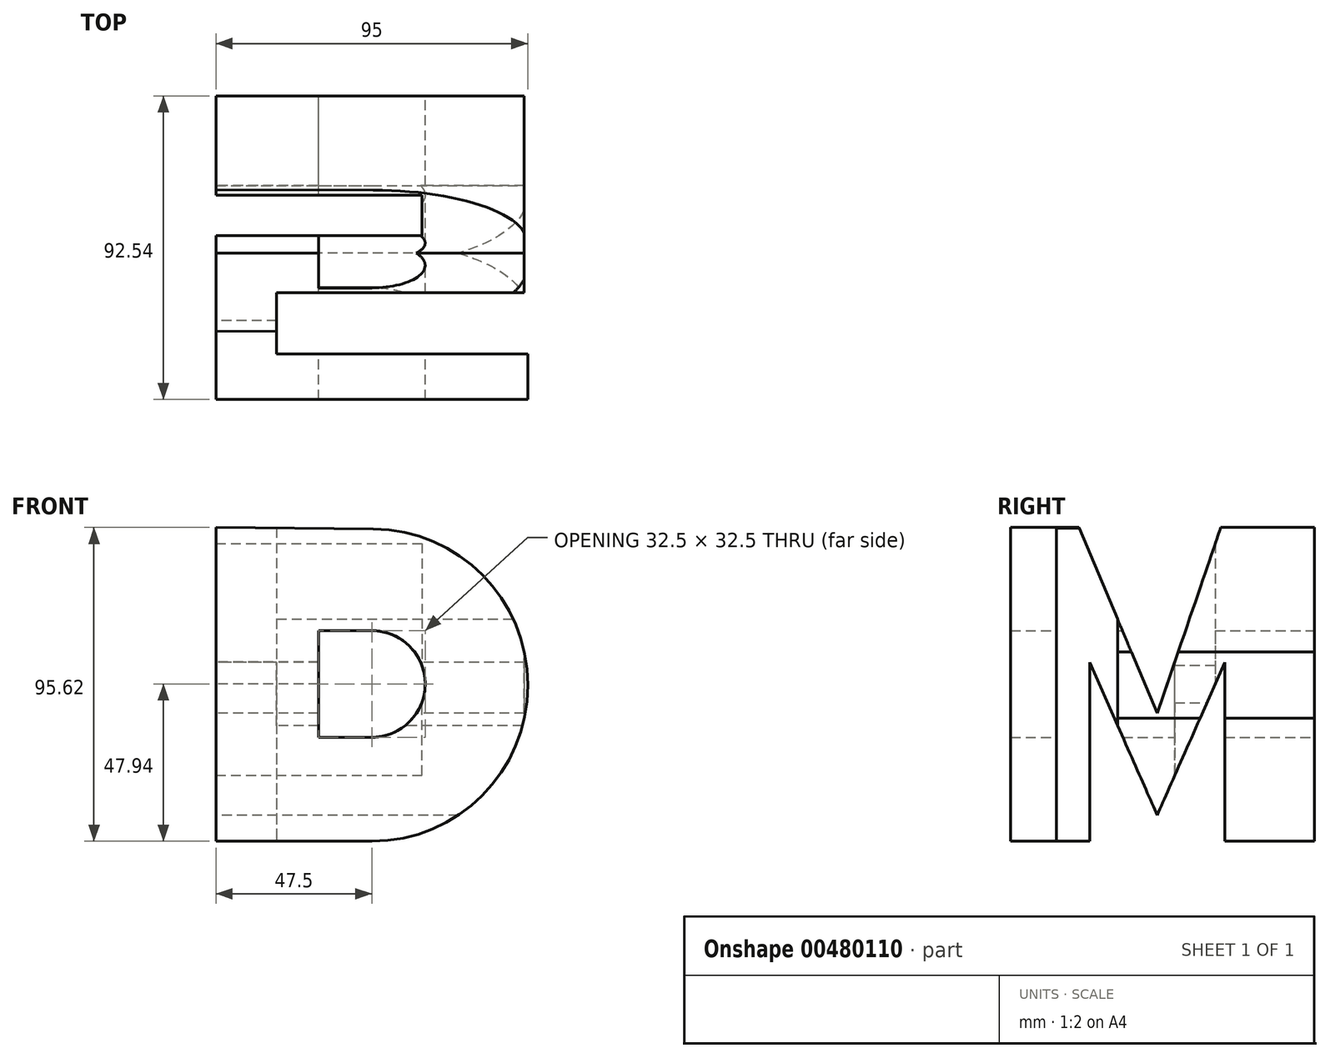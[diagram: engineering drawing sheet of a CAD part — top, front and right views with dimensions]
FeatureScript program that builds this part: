
annotation { "Feature Type Name" : "Feature", "Feature Type Description" : "" }
export const myFeature = defineFeature(function(context is Context, id is Id, definition is map)
    precondition{}
    {
        {
            var Q0;
            Q0=qCreatedBy(makeId("Top.planeOp"),FACE);
            var sketch = newSketch(context, id + "F0", { "sketchPlane" : qUnion([Q0])});
            skLineSegment(sketch, "E0.bottom", {"start": v(50, 50) * mm, "end": v(-50, 50) * mm, "construction": true});
            skLineSegment(sketch, "E0.top", {"start": v(50, -50) * mm, "end": v(-50, -50) * mm, "construction": true});
            skLineSegment(sketch, "E0.left", {"start": v(50, 50) * mm, "end": v(50, -50) * mm, "construction": true});
            skLineSegment(sketch, "E0.right", {"start": v(-50, 50) * mm, "end": v(-50, -50) * mm, "construction": true});
            skPoint(sketch, "E0.middle", {"position": v(0, 0) * mm});
            skLineSegment(sketch, "E1", {"start": v(30, -36.1) * mm, "end": v(-29, -36.1) * mm});
            skLineSegment(sketch, "E2", {"start": v(-29, -36.1) * mm, "end": v(-29, -17.46) * mm});
            skLineSegment(sketch, "E3", {"start": v(-29, -17.46) * mm, "end": v(30, -17.46) * mm});
            skLineSegment(sketch, "E4", {"start": v(30, 42.54) * mm, "end": v(-50, 42.54) * mm});
            skLineSegment(sketch, "E5", {"start": v(-50, 42.54) * mm, "end": v(-50, 12.32) * mm});
            skLineSegment(sketch, "E6", {"start": v(-50, 12.32) * mm, "end": v(15.22, 12.32) * mm});
            skLineSegment(sketch, "E7", {"start": v(15.22, 0) * mm, "end": v(-50, 0) * mm});
            skLineSegment(sketch, "E8", {"start": v(-50, 0) * mm, "end": v(-50, -50) * mm});
            skLineSegment(sketch, "E9", {"start": v(-50, -50) * mm, "end": v(30, -50) * mm});
            skLineSegment(sketch, "E10", {"start": v(15.22, 12.32) * mm, "end": v(15.22, 0) * mm});
            skLineSegment(sketch, "E11", {"start": v(30, -50) * mm, "end": v(50, -50) * mm});
            skLineSegment(sketch, "E12", {"start": v(30, -36.1) * mm, "end": v(50, -36.1) * mm});
            skLineSegment(sketch, "E13", {"start": v(50, -36.1) * mm, "end": v(50, -50) * mm});
            skLineSegment(sketch, "E14", {"start": v(30, -17.46) * mm, "end": v(46.44, -17.46) * mm});
            skLineSegment(sketch, "E15", {"start": v(46.44, -17.46) * mm, "end": v(46.44, 42.54) * mm});
            skLineSegment(sketch, "E16", {"start": v(46.44, 42.54) * mm, "end": v(30, 42.54) * mm});
            skPoint(sketch, "E17.orphan", {"position": v(30.69, 0) * mm});
            skSolve(sketch);
        }
        {
            var Q0;
            Q0=qCreatedBy(makeId("Front.planeOp"),FACE);
            var sketch = newSketch(context, id + "F1", { "sketchPlane" : qUnion([Q0])});
            skLineSegment(sketch, "E18.bottom", {"start": v(50, -50) * mm, "end": v(-50, -50) * mm, "construction": true});
            skLineSegment(sketch, "E18.top", {"start": v(50, 50) * mm, "end": v(-50, 50) * mm, "construction": true});
            skLineSegment(sketch, "E18.left", {"start": v(50, -50) * mm, "end": v(50, 50) * mm, "construction": true});
            skLineSegment(sketch, "E18.right", {"start": v(-50, -50) * mm, "end": v(-50, 50) * mm, "construction": true});
            skPoint(sketch, "E18.middle", {"position": v(0, 0) * mm});
            skLineSegment(sketch, "E19", {"start": v(-16.25, 16.25) * mm, "end": v(-16.25, -16.25) * mm});
            skLineSegment(sketch, "E20", {"start": v(-16.25, -16.25) * mm, "end": v(0, -16.25) * mm});
            skLineSegment(sketch, "E21", {"start": v(16.25, 0) * mm, "end": v(16.25, 0) * mm});
            skLineSegment(sketch, "E22", {"start": v(0, 16.25) * mm, "end": v(-16.25, 16.25) * mm});
            skLineSegment(sketch, "E23", {"start": v(-47.5, 47.68) * mm, "end": v(-47.5, -47.94) * mm});
            skLineSegment(sketch, "E24", {"start": v(-47.5, -47.94) * mm, "end": v(0, -47.94) * mm});
            skLineSegment(sketch, "E25", {"start": v(47.5, -0.44) * mm, "end": v(47.5, -0.22) * mm});
            skLineSegment(sketch, "E26", {"start": v(0.4, 47.28) * mm, "end": v(-47.5, 47.68) * mm});
            skPoint(sketch, "E27.visualSharp", {"position": v(16.25, 16.25) * mm});
            skArc(sketch, "E27.filletArc", {"start": v(16.25, 0) * mm, "mid": v(11.5, 11.5) * mm, "end": v(0, 16.25) * mm});
            skPoint(sketch, "E28.visualSharp", {"position": v(16.25, -16.25) * mm});
            skArc(sketch, "E28.filletArc", {"start": v(0, -16.25) * mm, "mid": v(11.5, -11.5) * mm, "end": v(16.25, 0) * mm});
            skPoint(sketch, "E29.visualSharp", {"position": v(47.5, 46.88) * mm});
            skArc(sketch, "E29.filletArc", {"start": v(47.5, -0.22) * mm, "mid": v(33.73, 33.23) * mm, "end": v(0.4, 47.28) * mm});
            skPoint(sketch, "E30.visualSharp", {"position": v(47.5, -47.94) * mm});
            skArc(sketch, "E30.filletArc", {"start": v(0, -47.94) * mm, "mid": v(33.59, -34.03) * mm, "end": v(47.5, -0.44) * mm});
            skSolve(sketch);
        }
        {
            var Q0;
            Q0=qCreatedBy(makeId("Right.planeOp"),FACE);
            var sketch = newSketch(context, id + "F2", { "sketchPlane" : qUnion([Q0])});
            skLineSegment(sketch, "E31.bottom", {"start": v(-55.72, -53.95) * mm, "end": v(55.72, -53.95) * mm, "construction": true});
            skLineSegment(sketch, "E31.top", {"start": v(-55.72, 57.5) * mm, "end": v(55.72, 57.5) * mm, "construction": true});
            skLineSegment(sketch, "E31.left", {"start": v(-55.72, -53.95) * mm, "end": v(-55.72, 57.5) * mm, "construction": true});
            skLineSegment(sketch, "E31.right", {"start": v(55.72, -53.95) * mm, "end": v(55.72, 57.5) * mm, "construction": true});
            skPoint(sketch, "E31.middle", {"position": v(0, 1.78) * mm});
            skLineSegment(sketch, "E32", {"start": v(-5.37, -8.96) * mm, "end": v(14.93, 50.45) * mm});
            skLineSegment(sketch, "E33", {"start": v(15.22, -50.64) * mm, "end": v(15.22, 6.57) * mm});
            skPoint(sketch, "E34.end.orphan", {"position": v(0, -33.43) * mm});
            skLineSegment(sketch, "E35", {"start": v(15.22, 6.57) * mm, "end": v(-5.37, -39.96) * mm});
            skLineSegment(sketch, "E36", {"start": v(-5.37, -39.96) * mm, "end": v(-25.97, 6.57) * mm});
            skLineSegment(sketch, "E37", {"start": v(-25.97, 6.57) * mm, "end": v(-25.97, -50.64) * mm});
            skLineSegment(sketch, "E38", {"start": v(-25.97, -50.64) * mm, "end": v(-55.72, -51.03) * mm});
            skLineSegment(sketch, "E39", {"start": v(-29.73, 48.9) * mm, "end": v(-5.37, -8.96) * mm});
            skLineSegment(sketch, "E40", {"start": v(-55.72, 48.9) * mm, "end": v(-55.72, -51.17) * mm});
            skLineSegment(sketch, "E41", {"start": v(14.93, 50.45) * mm, "end": v(55.72, 50.45) * mm});
            skLineSegment(sketch, "E42", {"start": v(55.72, 50.45) * mm, "end": v(55.72, -50.11) * mm});
            skLineSegment(sketch, "E43", {"start": v(55.72, -50.11) * mm, "end": v(15.22, -50.64) * mm});
            skPoint(sketch, "E44.start.orphan", {"position": v(-44.98, 50.45) * mm});
            skLineSegment(sketch, "E45", {"start": v(-55.72, 48.9) * mm, "end": v(-29.73, 48.9) * mm});
            skSolve(sketch);
        }
        {
            var Q0;
            Q0 = qSketchRegion(id + "F0", true);
            extrude(context, id + "F3", {"entities" : qUnion([Q0]), "endBound" : BoundingType.SYMMETRIC, "depth" : 100 * mm});
        }
        {
            var Q0;
            Q0 = qSketchRegion(id + "F1", true);
            extrude(context, id + "F4", {"entities" : qUnion([Q0]), "operationType" : NewBodyOperationType.INTERSECT, "endBound" : BoundingType.SYMMETRIC, "depth" : 100 * mm});
        }
        {
            var Q0;
            Q0 = qSketchRegion(id + "F2", true);
            extrude(context, id + "F5", {"entities" : qUnion([Q0]), "operationType" : NewBodyOperationType.INTERSECT, "endBound" : BoundingType.SYMMETRIC, "depth" : 100 * mm});
        }
    });
